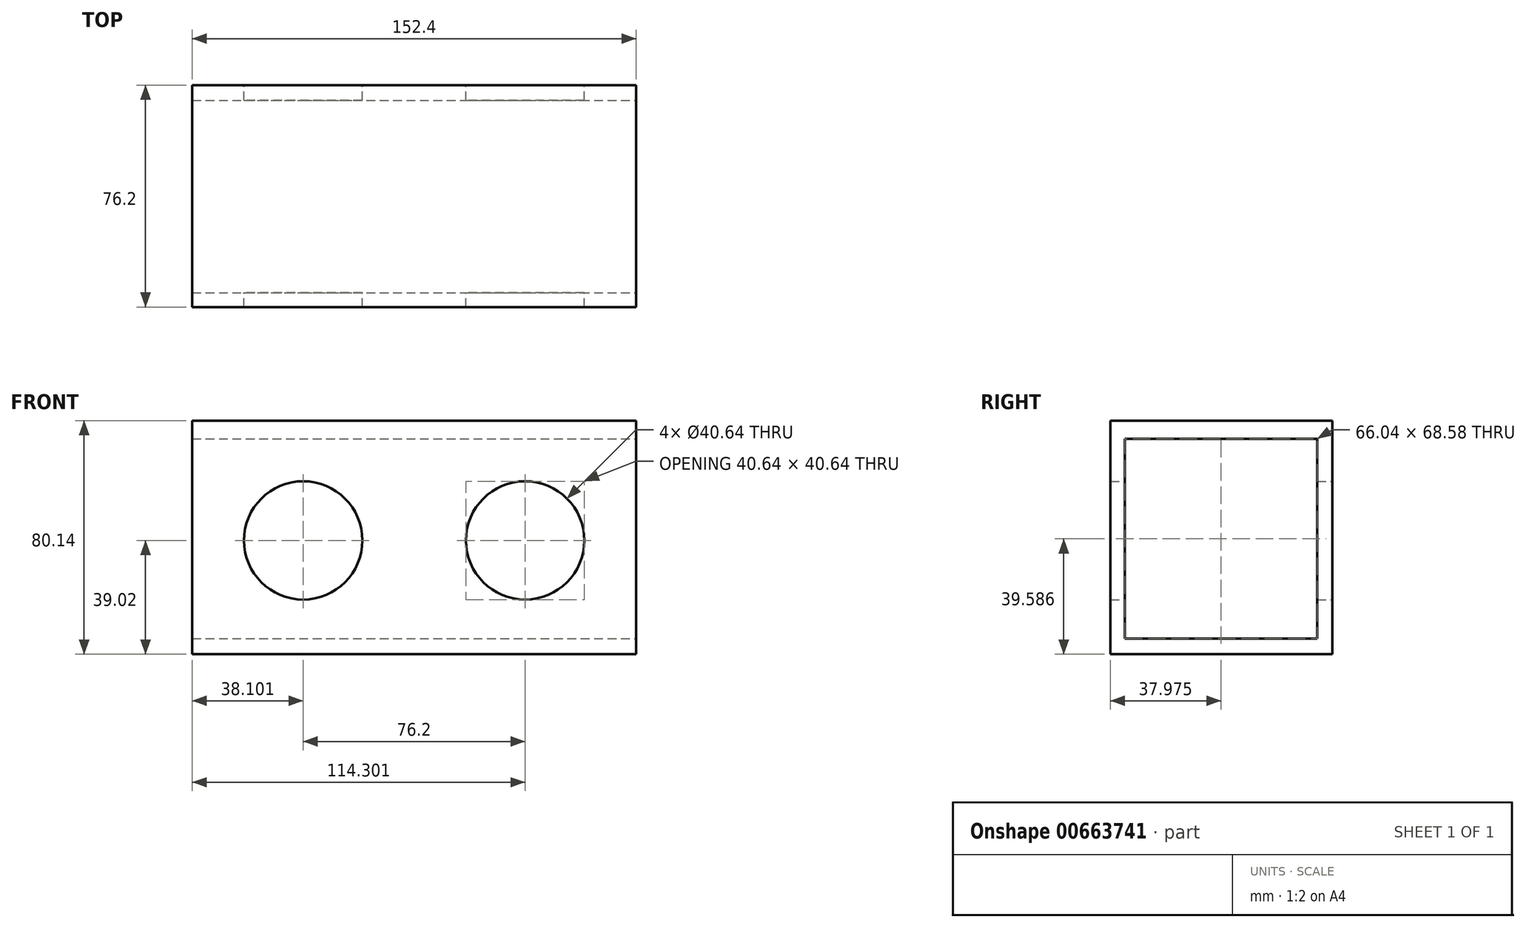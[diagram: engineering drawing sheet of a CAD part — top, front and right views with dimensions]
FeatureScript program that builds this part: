
annotation { "Feature Type Name" : "Feature", "Feature Type Description" : "" }
export const myFeature = defineFeature(function(context is Context, id is Id, definition is map)
    precondition{}
    {
        {
            var Q0;
            Q0=qCreatedBy(makeId("Front.planeOp"),FACE);
            var sketch = newSketch(context, id + "F0", { "sketchPlane" : qUnion([Q0])});
            skLineSegment(sketch, "E0.bottom", {"start": v(-74.18, 41.12) * mm, "end": v(78.22, 41.12) * mm});
            skLineSegment(sketch, "E0.top", {"start": v(-74.18, -39.02) * mm, "end": v(78.22, -39.02) * mm});
            skLineSegment(sketch, "E0.left", {"start": v(-74.18, 41.12) * mm, "end": v(-74.18, -39.02) * mm});
            skLineSegment(sketch, "E0.right", {"start": v(78.22, 41.12) * mm, "end": v(78.22, -39.02) * mm});
            skCircle(sketch, "E1", {"center": v(40.12, 0) * mm, "radius": 20.32 * mm});
            skCircle(sketch, "E2", {"center": v(-36.08, 0) * mm, "radius": 20.32 * mm});
            skSolve(sketch);
        }
        {
            var Q0;
            Q0=makeQuery(id+"F0.imprint","IMPRINT",FACE,{"disambiguationData":[TD([[makeQuery(id+"F0.imprint","IMPRINT",EDGE,{"derivedFrom":sQuery(id+"F0.wireOp",EDGE,"E0.bottom")}),-1.0]])]});
            extrude(context, id + "F1", {"entities" : qUnion([Q0]), "depth" : 76.2 * mm, "offsetDistance" : 25.4 * mm});
        }
        {
            var Q0;
            Q0=qCreatedBy(makeId("Right.planeOp"),FACE);
            var sketch = newSketch(context, id + "F2", { "sketchPlane" : qUnion([Q0])});
            skLineSegment(sketch, "E3.bottom", {"start": v(-71.24, 34.86) * mm, "end": v(-5.2, 34.86) * mm});
            skLineSegment(sketch, "E3.top", {"start": v(-71.24, -33.72) * mm, "end": v(-5.2, -33.72) * mm});
            skLineSegment(sketch, "E3.left", {"start": v(-71.24, 34.86) * mm, "end": v(-71.24, -33.72) * mm});
            skLineSegment(sketch, "E3.right", {"start": v(-5.2, 34.86) * mm, "end": v(-5.2, -33.72) * mm});
            skSolve(sketch);
        }
        {
            var Q0;
            Q0=sQuery(id+"F2.wireOp",EDGE,"E3.bottom");
            var Q1;
            Q1=sQuery(id+"F2.wireOp",EDGE,"E3.right");
            var Q2;
            Q2=sQuery(id+"F2.wireOp",EDGE,"E3.left");
            var Q3;
            Q3=sQuery(id+"F2.wireOp",EDGE,"E3.top");
            extrude(context, id + "F3", {"bodyType" : ToolBodyType.SURFACE, "surfaceEntities" : qUnion([Q0, Q1, Q2, Q3]), "depth" : 25.4 * mm, "offsetDistance" : 25.4 * mm});
        }
        {
            var Q0;
            Q0 = qSketchRegion(id + "F2", true);
            extrude(context, id + "F4", {"entities" : qUnion([Q0]), "operationType" : NewBodyOperationType.REMOVE, "oppositeDirection" : true, "depth" : 203.2 * mm, "offsetDistance" : 25.4 * mm});
        }
        {
            var Q0;
            Q0=makeQuery(id+"F4.boolean.opBoolean","COPY",FACE,{"derivedFrom":makeQuery(id+"F4.opExtrude","CAP_FACE",FACE,{"disambiguationData":[OSD([sQuery(id+"F2.wireOp",EDGE,"E3.bottom"),sQuery(id+"F2.wireOp",EDGE,"E3.top"),sQuery(id+"F2.wireOp",EDGE,"E3.left"),sQuery(id+"F2.wireOp",EDGE,"E3.right")])],"isStart":true})});
            extrude(context, id + "F5", {"entities" : qUnion([Q0]), "operationType" : NewBodyOperationType.REMOVE, "oppositeDirection" : true, "depth" : 203.2 * mm, "offsetDistance" : 25.4 * mm});
        }
        {
            var Q0;
            Q0=qCreatedBy(makeId("Top.planeOp"),FACE);
            var sketch = newSketch(context, id + "F6", { "sketchPlane" : qUnion([Q0])});
            skLineSegment(sketch, "E4.bottom", {"start": v(-36.55, -27.33) * mm, "end": v(40.67, -27.33) * mm});
            skLineSegment(sketch, "E4.top", {"start": v(-36.55, -47.8) * mm, "end": v(40.67, -47.8) * mm});
            skLineSegment(sketch, "E4.left", {"start": v(-36.55, -27.33) * mm, "end": v(-36.55, -47.8) * mm});
            skLineSegment(sketch, "E4.right", {"start": v(40.67, -27.33) * mm, "end": v(40.67, -47.8) * mm});
            skSolve(sketch);
        }
        {
            var Q0;
            Q0 = qSketchRegion(id + "F6", true);
            extrude(context, id + "F7", {"entities" : qUnion([Q0]), "operationType" : NewBodyOperationType.REMOVE, "oppositeDirection" : true, "depth" : 25.4 * mm, "offsetDistance" : 25.4 * mm});
        }
    });
